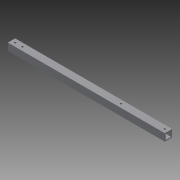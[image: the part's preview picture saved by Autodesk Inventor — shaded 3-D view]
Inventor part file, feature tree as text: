
AUTODESK INVENTOR PART (.ipt)
format: ipt  version: 2015 SP1 (Build 190203100, 203)  size: 102,912 bytes
history: native  units: in
note: dims shown in document units (in); Inventor stores cm internally (conversion verified against a paired STEP export)
features: sketch x3, hole x2, projected_geometry x2, extrude x1
ambient origin geometry x8: Origin, YZ Plane, XZ Plane, XY Plane, X Axis, Y Axis, Z Axis, Center Point
bodies: Solid1 (feature_tree)
feature tree (8):
  extrude  "Extrusion1"  Depth=1.0in
  hole  "Hole1"  [1 undecoded]
  hole  "Hole2"  [1 undecoded]
  sketch  "Sketch1"  dims[d0=1.0in d1=1.0in]
  sketch  "Sketch2"  dims[d2=0.75in d3=0.75in]
  projected_geometry  "Projected Loop1"
  sketch  "Sketch3"  dims[d4=0.125in d5=0.125in d6=21.5in d7=0.0in d8=0.5in d9=0.5in d10=0.5in d11=0.5in d12=0.25in d13=0.75in d14=0.375in d15=0.25in d16=0.5635in d17=1.0in d18=0.8108in d19=6.5in d20=1.5in d21=0.5in d22=0.5in d23=0.25in d24=0.75in d25=0.375in d26=0.25in d27=0.5635in d28=1.0in d29=0.8108in]
  projected_geometry  "Projected Loop2"
note: 2 required parameter values undecoded (feature->parameter linkage not recoverable at this tier; creation-order binding heuristic only, values carry confidence <= 0.55)
